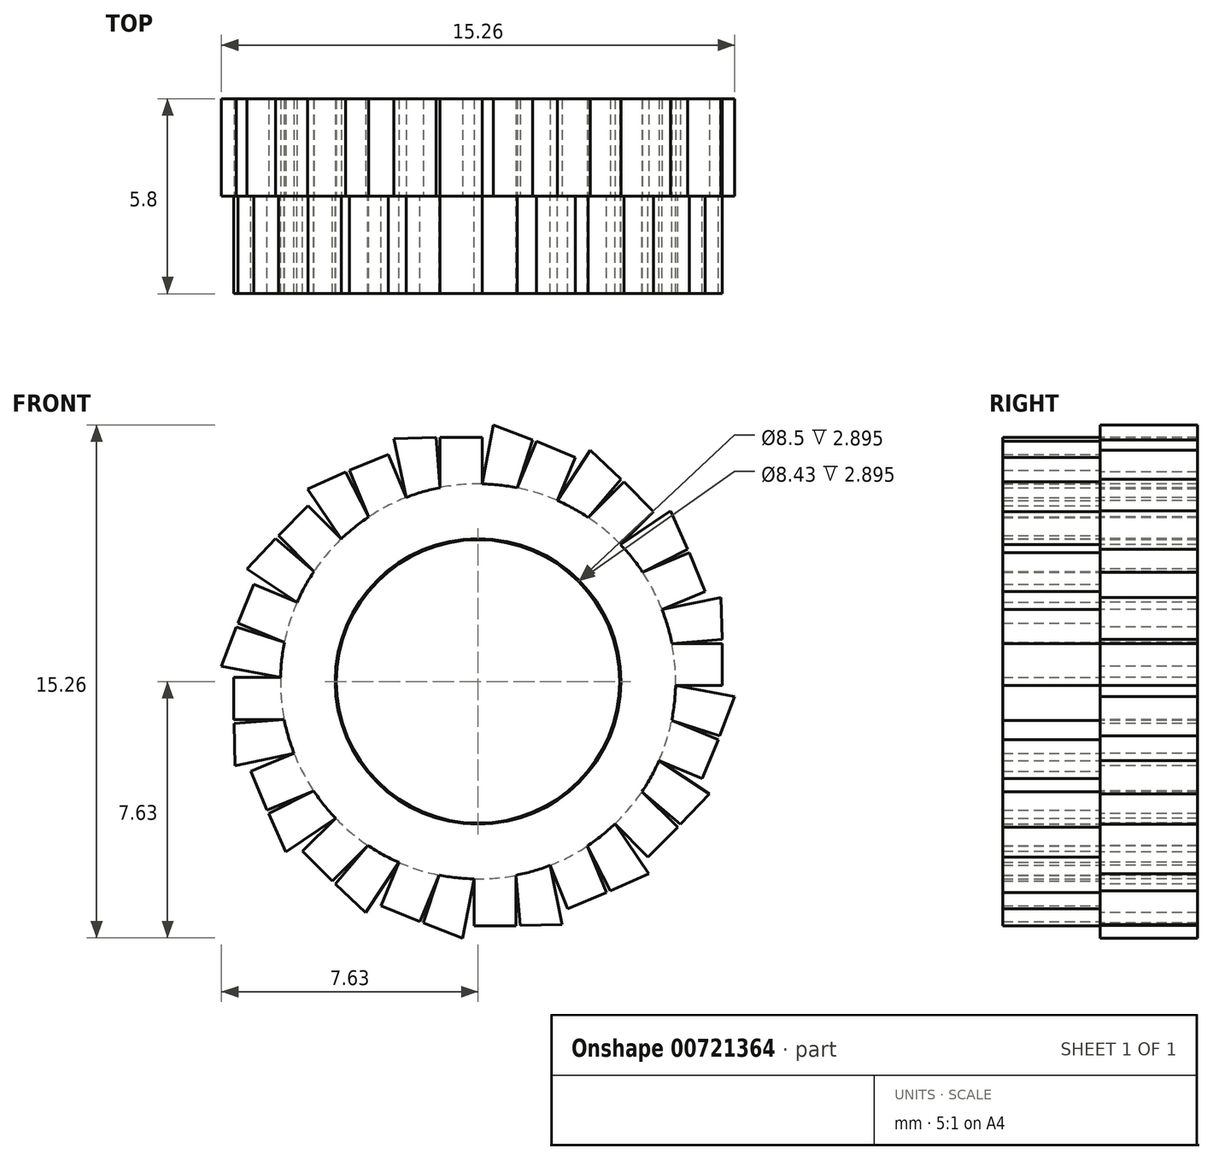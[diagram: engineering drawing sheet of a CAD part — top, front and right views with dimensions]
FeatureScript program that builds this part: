
annotation { "Feature Type Name" : "Feature", "Feature Type Description" : "" }
export const myFeature = defineFeature(function(context is Context, id is Id, definition is map)
    precondition{}
    {
        {
            var Q0;
            Q0=qCreatedBy(makeId("Front.planeOp"),FACE);
            var sketch = newSketch(context, id + "F0", { "sketchPlane" : qUnion([Q0])});
            skCircle(sketch, "E0", {"center": v(0, 0) * mm, "radius": 4.25 * mm});
            skCircle(sketch, "E1", {"center": v(0, 0) * mm, "radius": 5.88 * mm});
            skLineSegment(sketch, "E2", {"start": v(-1.13, 5.77) * mm, "end": v(-1.13, 7.27) * mm});
            skLineSegment(sketch, "E3", {"start": v(-1.13, 7.27) * mm, "end": v(0.12, 7.27) * mm});
            skLineSegment(sketch, "E4", {"start": v(0.12, 7.27) * mm, "end": v(0.12, 5.87) * mm});
            skLineSegment(sketch, "E5.1.0", {"start": v(-3.25, 4.9) * mm, "end": v(-3.83, 6.28) * mm});
            skLineSegment(sketch, "E5.1.1", {"start": v(-3.83, 6.28) * mm, "end": v(-2.67, 6.76) * mm});
            skLineSegment(sketch, "E5.1.2", {"start": v(-2.67, 6.76) * mm, "end": v(-2.14, 5.47) * mm});
            skLineSegment(sketch, "E5.2.0", {"start": v(-4.88, 3.28) * mm, "end": v(-5.94, 4.34) * mm});
            skLineSegment(sketch, "E5.2.1", {"start": v(-5.94, 4.34) * mm, "end": v(-5.05, 5.22) * mm});
            skLineSegment(sketch, "E5.2.2", {"start": v(-5.05, 5.22) * mm, "end": v(-4.07, 4.24) * mm});
            skLineSegment(sketch, "E5.3.0", {"start": v(-5.76, 1.16) * mm, "end": v(-7.14, 1.73) * mm});
            skLineSegment(sketch, "E5.3.1", {"start": v(-7.14, 1.73) * mm, "end": v(-6.67, 2.89) * mm});
            skLineSegment(sketch, "E5.3.2", {"start": v(-6.67, 2.89) * mm, "end": v(-5.38, 2.36) * mm});
            skLineSegment(sketch, "E5.4.0", {"start": v(-5.77, -1.13) * mm, "end": v(-7.27, -1.13) * mm});
            skLineSegment(sketch, "E5.4.1", {"start": v(-7.27, -1.13) * mm, "end": v(-7.27, 0.12) * mm});
            skLineSegment(sketch, "E5.4.2", {"start": v(-7.27, 0.12) * mm, "end": v(-5.87, 0.12) * mm});
            skLineSegment(sketch, "E5.5.0", {"start": v(-4.9, -3.25) * mm, "end": v(-6.28, -3.83) * mm});
            skLineSegment(sketch, "E5.5.1", {"start": v(-6.28, -3.83) * mm, "end": v(-6.76, -2.67) * mm});
            skLineSegment(sketch, "E5.5.2", {"start": v(-6.76, -2.67) * mm, "end": v(-5.47, -2.14) * mm});
            skLineSegment(sketch, "E5.6.0", {"start": v(-3.28, -4.88) * mm, "end": v(-4.34, -5.94) * mm});
            skLineSegment(sketch, "E5.6.1", {"start": v(-4.34, -5.94) * mm, "end": v(-5.22, -5.05) * mm});
            skLineSegment(sketch, "E5.6.2", {"start": v(-5.22, -5.05) * mm, "end": v(-4.24, -4.07) * mm});
            skLineSegment(sketch, "E5.7.0", {"start": v(-1.16, -5.76) * mm, "end": v(-1.73, -7.14) * mm});
            skLineSegment(sketch, "E5.7.1", {"start": v(-1.73, -7.14) * mm, "end": v(-2.89, -6.67) * mm});
            skLineSegment(sketch, "E5.7.2", {"start": v(-2.89, -6.67) * mm, "end": v(-2.36, -5.38) * mm});
            skLineSegment(sketch, "E5.8.0", {"start": v(1.13, -5.77) * mm, "end": v(1.13, -7.27) * mm});
            skLineSegment(sketch, "E5.8.1", {"start": v(1.13, -7.27) * mm, "end": v(-0.12, -7.27) * mm});
            skLineSegment(sketch, "E5.8.2", {"start": v(-0.12, -7.27) * mm, "end": v(-0.12, -5.87) * mm});
            skLineSegment(sketch, "E5.9.0", {"start": v(3.25, -4.9) * mm, "end": v(3.83, -6.28) * mm});
            skLineSegment(sketch, "E5.9.1", {"start": v(3.83, -6.28) * mm, "end": v(2.67, -6.76) * mm});
            skLineSegment(sketch, "E5.9.2", {"start": v(2.67, -6.76) * mm, "end": v(2.14, -5.47) * mm});
            skLineSegment(sketch, "E5.10.0", {"start": v(4.88, -3.28) * mm, "end": v(5.94, -4.34) * mm});
            skLineSegment(sketch, "E5.10.1", {"start": v(5.94, -4.34) * mm, "end": v(5.05, -5.22) * mm});
            skLineSegment(sketch, "E5.10.2", {"start": v(5.05, -5.22) * mm, "end": v(4.07, -4.24) * mm});
            skLineSegment(sketch, "E5.11.0", {"start": v(5.76, -1.16) * mm, "end": v(7.14, -1.73) * mm});
            skLineSegment(sketch, "E5.11.1", {"start": v(7.14, -1.73) * mm, "end": v(6.67, -2.89) * mm});
            skLineSegment(sketch, "E5.11.2", {"start": v(6.67, -2.89) * mm, "end": v(5.38, -2.36) * mm});
            skLineSegment(sketch, "E5.12.0", {"start": v(5.77, 1.13) * mm, "end": v(7.27, 1.13) * mm});
            skLineSegment(sketch, "E5.12.1", {"start": v(7.27, 1.13) * mm, "end": v(7.27, -0.12) * mm});
            skLineSegment(sketch, "E5.12.2", {"start": v(7.27, -0.12) * mm, "end": v(5.87, -0.12) * mm});
            skLineSegment(sketch, "E5.13.0", {"start": v(4.9, 3.25) * mm, "end": v(6.28, 3.83) * mm});
            skLineSegment(sketch, "E5.13.1", {"start": v(6.28, 3.83) * mm, "end": v(6.76, 2.67) * mm});
            skLineSegment(sketch, "E5.13.2", {"start": v(6.76, 2.67) * mm, "end": v(5.47, 2.14) * mm});
            skLineSegment(sketch, "E5.14.0", {"start": v(3.28, 4.88) * mm, "end": v(4.34, 5.94) * mm});
            skLineSegment(sketch, "E5.14.1", {"start": v(4.34, 5.94) * mm, "end": v(5.22, 5.05) * mm});
            skLineSegment(sketch, "E5.14.2", {"start": v(5.22, 5.05) * mm, "end": v(4.24, 4.07) * mm});
            skLineSegment(sketch, "E5.15.0", {"start": v(1.16, 5.76) * mm, "end": v(1.73, 7.14) * mm});
            skLineSegment(sketch, "E5.15.1", {"start": v(1.73, 7.14) * mm, "end": v(2.89, 6.67) * mm});
            skLineSegment(sketch, "E5.15.2", {"start": v(2.89, 6.67) * mm, "end": v(2.36, 5.38) * mm});
            skSolve(sketch);
        }
        {
            var Q0;
            Q0 = qSketchRegion(id + "F0", true);
            extrude(context, id + "F1", {"entities" : qUnion([Q0]), "depth" : 2.9 * mm, "offsetDistance" : 25 * mm});
        }
        {
            var Q0;
            Q0 = qSketchRegion(id + "F0", true);
            extrude(context, id + "F2", {"entities" : qUnion([Q0]), "operationType" : NewBodyOperationType.ADD, "depth" : 2.9 * mm, "offsetDistance" : 25 * mm});
        }
        {
            var Q0;
            Q0 = qSketchRegion(id + "F0", true);
            extrude(context, id + "F3", {"entities" : qUnion([Q0]), "operationType" : NewBodyOperationType.ADD, "depth" : 2.9 * mm, "offsetDistance" : 25 * mm});
        }
        {
            var Q0;
            Q0=makeQuery(id+"F1.opExtrude","CAP_FACE",FACE,{"disambiguationData":[OSD([sQuery(id+"F0.wireOp",EDGE,"E0"),sQuery(id+"F0.wireOp",EDGE,"E1"),sQuery(id+"F0.wireOp",EDGE,"E2"),sQuery(id+"F0.wireOp",EDGE,"E3"),sQuery(id+"F0.wireOp",EDGE,"E4"),sQuery(id+"F0.wireOp",EDGE,"E5.1.0"),sQuery(id+"F0.wireOp",EDGE,"E5.1.1"),sQuery(id+"F0.wireOp",EDGE,"E5.1.2"),sQuery(id+"F0.wireOp",EDGE,"E5.2.0"),sQuery(id+"F0.wireOp",EDGE,"E5.2.1"),sQuery(id+"F0.wireOp",EDGE,"E5.2.2"),sQuery(id+"F0.wireOp",EDGE,"E5.3.0"),sQuery(id+"F0.wireOp",EDGE,"E5.3.1"),sQuery(id+"F0.wireOp",EDGE,"E5.3.2"),sQuery(id+"F0.wireOp",EDGE,"E5.4.0"),sQuery(id+"F0.wireOp",EDGE,"E5.4.1"),sQuery(id+"F0.wireOp",EDGE,"E5.4.2"),sQuery(id+"F0.wireOp",EDGE,"E5.5.0"),sQuery(id+"F0.wireOp",EDGE,"E5.5.1"),sQuery(id+"F0.wireOp",EDGE,"E5.5.2"),sQuery(id+"F0.wireOp",EDGE,"E5.6.0"),sQuery(id+"F0.wireOp",EDGE,"E5.6.1"),sQuery(id+"F0.wireOp",EDGE,"E5.6.2"),sQuery(id+"F0.wireOp",EDGE,"E5.7.0"),sQuery(id+"F0.wireOp",EDGE,"E5.7.1"),sQuery(id+"F0.wireOp",EDGE,"E5.7.2"),sQuery(id+"F0.wireOp",EDGE,"E5.8.0"),sQuery(id+"F0.wireOp",EDGE,"E5.8.1"),sQuery(id+"F0.wireOp",EDGE,"E5.8.2"),sQuery(id+"F0.wireOp",EDGE,"E5.9.0"),sQuery(id+"F0.wireOp",EDGE,"E5.9.1"),sQuery(id+"F0.wireOp",EDGE,"E5.9.2"),sQuery(id+"F0.wireOp",EDGE,"E5.10.0"),sQuery(id+"F0.wireOp",EDGE,"E5.10.1"),sQuery(id+"F0.wireOp",EDGE,"E5.10.2"),sQuery(id+"F0.wireOp",EDGE,"E5.11.0"),sQuery(id+"F0.wireOp",EDGE,"E5.11.1"),sQuery(id+"F0.wireOp",EDGE,"E5.11.2"),sQuery(id+"F0.wireOp",EDGE,"E5.12.0"),sQuery(id+"F0.wireOp",EDGE,"E5.12.1"),sQuery(id+"F0.wireOp",EDGE,"E5.12.2"),sQuery(id+"F0.wireOp",EDGE,"E5.13.0"),sQuery(id+"F0.wireOp",EDGE,"E5.13.1"),sQuery(id+"F0.wireOp",EDGE,"E5.13.2"),sQuery(id+"F0.wireOp",EDGE,"E5.14.0"),sQuery(id+"F0.wireOp",EDGE,"E5.14.1"),sQuery(id+"F0.wireOp",EDGE,"E5.14.2"),sQuery(id+"F0.wireOp",EDGE,"E5.15.0"),sQuery(id+"F0.wireOp",EDGE,"E5.15.1"),sQuery(id+"F0.wireOp",EDGE,"E5.15.2")])],"isStart":true});
            var sketch = newSketch(context, id + "F4", { "sketchPlane" : qUnion([Q0])});
            skPoint(sketch, "E6.start.orphan", {"position": v(0, 8.1) * mm});
            skPoint(sketch, "E7.end.orphan", {"position": v(0, 9.7) * mm});
            skPoint(sketch, "E8.start.orphan", {"position": v(-1.16, 7.14) * mm});
            skPoint(sketch, "E9.endSnap0", {"position": v(-1.45, 6.45) * mm});
            skPoint(sketch, "E10.end.orphan", {"position": v(-0.12, 8.13) * mm});
            skPoint(sketch, "E11.end.orphan", {"position": v(-0.12, 5.87) * mm});
            skPoint(sketch, "E11.start.orphan", {"position": v(-0.68, 7.27) * mm});
            skPoint(sketch, "E12.end.orphan", {"position": v(0, 8.97) * mm});
            skPoint(sketch, "E9.end.orphan", {"position": v(-1.45, 7.95) * mm});
            skCircle(sketch, "E13", {"center": v(0, 0) * mm, "radius": 4.21 * mm});
            skCircle(sketch, "E14", {"center": v(0, 0) * mm, "radius": 5.88 * mm});
            skPoint(sketch, "E15.endSnap0", {"position": v(4.73, -4.56) * mm});
            skPoint(sketch, "E16.start.orphan", {"position": v(6.38, -5.05) * mm});
            skPoint(sketch, "E15.end.orphan", {"position": v(6.73, -4.56) * mm});
            skPoint(sketch, "E17.start.orphan", {"position": v(5.59, 6.28) * mm});
            skLineSegment(sketch, "E18", {"start": v(4.88, 3.28) * mm, "end": v(6.02, 4.25) * mm});
            skPoint(sketch, "E19.end.orphan", {"position": v(7.63, 3.28) * mm});
            skLineSegment(sketch, "E20", {"start": v(5.38, 2.36) * mm, "end": v(6.88, 3.34) * mm});
            skLineSegment(sketch, "E21", {"start": v(6.88, 3.34) * mm, "end": v(6.02, 4.25) * mm});
            skLineSegment(sketch, "E22.1.0", {"start": v(3.25, 4.9) * mm, "end": v(3.93, 6.23) * mm});
            skLineSegment(sketch, "E22.1.1", {"start": v(5.08, 5.72) * mm, "end": v(3.93, 6.23) * mm});
            skLineSegment(sketch, "E22.1.2", {"start": v(4.07, 4.24) * mm, "end": v(5.08, 5.72) * mm});
            skLineSegment(sketch, "E22.2.0", {"start": v(1.13, 5.77) * mm, "end": v(1.25, 7.26) * mm});
            skLineSegment(sketch, "E22.2.1", {"start": v(2.5, 7.23) * mm, "end": v(1.25, 7.26) * mm});
            skLineSegment(sketch, "E22.2.2", {"start": v(2.14, 5.47) * mm, "end": v(2.5, 7.23) * mm});
            skLineSegment(sketch, "E22.3.0", {"start": v(-1.16, 5.76) * mm, "end": v(-1.62, 7.19) * mm});
            skLineSegment(sketch, "E22.3.1", {"start": v(-0.45, 7.63) * mm, "end": v(-1.62, 7.19) * mm});
            skLineSegment(sketch, "E22.3.2", {"start": v(-0.12, 5.87) * mm, "end": v(-0.45, 7.63) * mm});
            skLineSegment(sketch, "E22.4.0", {"start": v(-3.28, 4.88) * mm, "end": v(-4.25, 6.02) * mm});
            skLineSegment(sketch, "E22.4.1", {"start": v(-3.34, 6.88) * mm, "end": v(-4.25, 6.02) * mm});
            skLineSegment(sketch, "E22.4.2", {"start": v(-2.36, 5.38) * mm, "end": v(-3.34, 6.88) * mm});
            skLineSegment(sketch, "E22.5.0", {"start": v(-4.9, 3.25) * mm, "end": v(-6.23, 3.93) * mm});
            skLineSegment(sketch, "E22.5.1", {"start": v(-5.72, 5.08) * mm, "end": v(-6.23, 3.93) * mm});
            skLineSegment(sketch, "E22.5.2", {"start": v(-4.24, 4.07) * mm, "end": v(-5.72, 5.08) * mm});
            skLineSegment(sketch, "E22.6.0", {"start": v(-5.77, 1.13) * mm, "end": v(-7.26, 1.25) * mm});
            skLineSegment(sketch, "E22.6.1", {"start": v(-7.23, 2.5) * mm, "end": v(-7.26, 1.25) * mm});
            skLineSegment(sketch, "E22.6.2", {"start": v(-5.47, 2.14) * mm, "end": v(-7.23, 2.5) * mm});
            skLineSegment(sketch, "E22.7.0", {"start": v(-5.76, -1.16) * mm, "end": v(-7.19, -1.62) * mm});
            skLineSegment(sketch, "E22.7.1", {"start": v(-7.63, -0.45) * mm, "end": v(-7.19, -1.62) * mm});
            skLineSegment(sketch, "E22.7.2", {"start": v(-5.87, -0.12) * mm, "end": v(-7.63, -0.45) * mm});
            skLineSegment(sketch, "E22.8.0", {"start": v(-4.88, -3.28) * mm, "end": v(-6.02, -4.25) * mm});
            skLineSegment(sketch, "E22.8.1", {"start": v(-6.88, -3.34) * mm, "end": v(-6.02, -4.25) * mm});
            skLineSegment(sketch, "E22.8.2", {"start": v(-5.38, -2.36) * mm, "end": v(-6.88, -3.34) * mm});
            skLineSegment(sketch, "E22.9.0", {"start": v(-3.25, -4.9) * mm, "end": v(-3.93, -6.23) * mm});
            skLineSegment(sketch, "E22.9.1", {"start": v(-5.08, -5.72) * mm, "end": v(-3.93, -6.23) * mm});
            skLineSegment(sketch, "E22.9.2", {"start": v(-4.07, -4.24) * mm, "end": v(-5.08, -5.72) * mm});
            skLineSegment(sketch, "E22.10.0", {"start": v(-1.13, -5.77) * mm, "end": v(-1.25, -7.26) * mm});
            skLineSegment(sketch, "E22.10.1", {"start": v(-2.5, -7.23) * mm, "end": v(-1.25, -7.26) * mm});
            skLineSegment(sketch, "E22.10.2", {"start": v(-2.14, -5.47) * mm, "end": v(-2.5, -7.23) * mm});
            skLineSegment(sketch, "E22.11.0", {"start": v(1.16, -5.76) * mm, "end": v(1.62, -7.19) * mm});
            skLineSegment(sketch, "E22.11.1", {"start": v(0.45, -7.63) * mm, "end": v(1.62, -7.19) * mm});
            skLineSegment(sketch, "E22.11.2", {"start": v(0.12, -5.87) * mm, "end": v(0.45, -7.63) * mm});
            skLineSegment(sketch, "E22.12.0", {"start": v(3.28, -4.88) * mm, "end": v(4.25, -6.02) * mm});
            skLineSegment(sketch, "E22.12.1", {"start": v(3.34, -6.88) * mm, "end": v(4.25, -6.02) * mm});
            skLineSegment(sketch, "E22.12.2", {"start": v(2.36, -5.38) * mm, "end": v(3.34, -6.88) * mm});
            skLineSegment(sketch, "E22.13.0", {"start": v(4.9, -3.25) * mm, "end": v(6.23, -3.93) * mm});
            skLineSegment(sketch, "E22.13.1", {"start": v(5.72, -5.08) * mm, "end": v(6.23, -3.93) * mm});
            skLineSegment(sketch, "E22.13.2", {"start": v(4.24, -4.07) * mm, "end": v(5.72, -5.08) * mm});
            skLineSegment(sketch, "E22.14.0", {"start": v(5.77, -1.13) * mm, "end": v(7.26, -1.25) * mm});
            skLineSegment(sketch, "E22.14.1", {"start": v(7.23, -2.5) * mm, "end": v(7.26, -1.25) * mm});
            skLineSegment(sketch, "E22.14.2", {"start": v(5.47, -2.14) * mm, "end": v(7.23, -2.5) * mm});
            skLineSegment(sketch, "E22.15.0", {"start": v(5.76, 1.16) * mm, "end": v(7.19, 1.62) * mm});
            skLineSegment(sketch, "E22.15.1", {"start": v(7.63, 0.45) * mm, "end": v(7.19, 1.62) * mm});
            skLineSegment(sketch, "E22.15.2", {"start": v(5.87, 0.12) * mm, "end": v(7.63, 0.45) * mm});
            skSolve(sketch);
        }
        {
            var Q0;
            Q0 = qSketchRegion(id + "F4", true);
            extrude(context, id + "F5", {"entities" : qUnion([Q0]), "operationType" : NewBodyOperationType.ADD, "depth" : 2.9 * mm, "offsetDistance" : 25 * mm});
        }
    });
